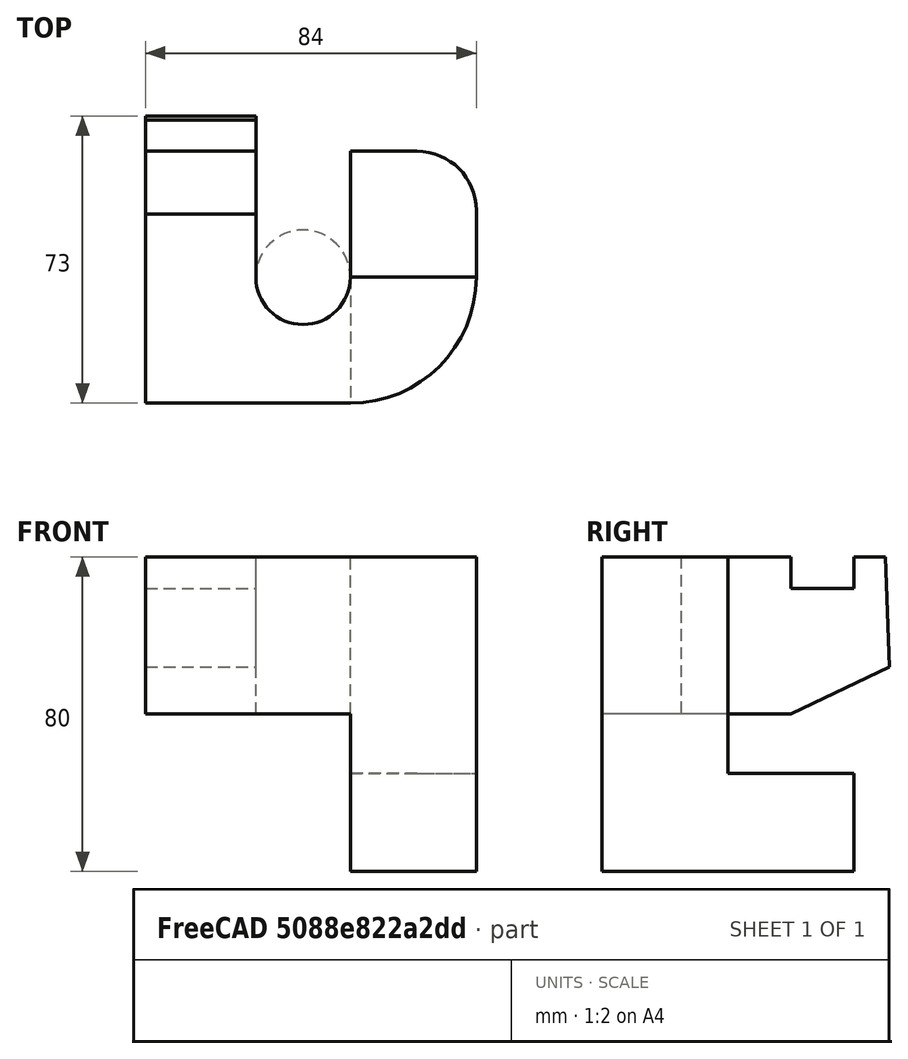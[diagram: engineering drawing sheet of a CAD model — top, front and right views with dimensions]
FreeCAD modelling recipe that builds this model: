
FCSTD DOCUMENT  (FreeCAD 0.18R4 (GitTag))
Label: Ass1 2nd sem
License: All rights reserved
LicenseURL: http://en.wikipedia.org/wiki/All_rights_reserved
objects: TechDraw::DrawViewDimension×14, Sketcher::SketchObject×4, PartDesign::Pad×4, TechDraw::DrawProjGroupItem×3, TechDraw::DrawProjGroup×3, TechDraw::DrawViewAnnotation×3, PartDesign::Pocket×1, PartDesign::Body×1, TechDraw::DrawSVGTemplate×1, TechDraw::DrawPage×1
note: 15 computed .brp shape members not serialized (recipe doc carries the construction recipe); baked Part::Feature solids carry a one-line shape summary decoded from their .brp

FEATURE [Sketcher::SketchObject] Sketch
  MapMode = 5
  Support = -> [XY_Plane]
  sketch-geometry (7):
    g0: LineSegment StartX=28 StartY=32 StartZ=0 EndX=28 EndY=48 EndZ=0
    g1: LineSegment StartX=28 StartY=48 StartZ=0 EndX=0 EndY=48 EndZ=0
    g2: LineSegment StartX=0 StartY=48 StartZ=0 EndX=0 EndY=0 EndZ=0
    g3: LineSegment StartX=0 StartY=0 StartZ=0 EndX=52 EndY=0 EndZ=0
    g4: LineSegment StartX=84 StartY=32 StartZ=0 EndX=52 EndY=32 EndZ=0
    g5: ArcOfCircle CenterX=52 CenterY=32 CenterZ=0 NormalX=0 NormalY=0 NormalZ=1 AngleXU=0 Radius=32 StartAngle=4.71239 EndAngle=6.28319
    g6: ArcOfCircle CenterX=40 CenterY=32 CenterZ=0 NormalX=0 NormalY=0 NormalZ=1 AngleXU=0 Radius=12 StartAngle=3.14159 EndAngle=6.28319
  constraints (20):
    c: Coincident(g0,g1)
    c: Coincident(g1,g2)
    c: Coincident(g2,g3)
    c: Parallel(g1,g4)
    c: Parallel(g4,g3)
    c: Parallel(g3,g-1)
    c: Parallel(g2,g0)
    c: Tangent(g3,g5) = -1.5708
    c: Coincident(g4,g5)
    c: Radius(g5) = 32
    c: Coincident(g-1,g2)
    c: PointOnObject(g1,g-2)
    c: DistanceX(g2,g4) = 84
    c: DistanceY(g2,g2) = 48
    c: DistanceX(g1,g1) = 28
    c: Coincident(g5,g4)
    c: DistanceY(g0,g0) = 16
    c: Radius(g6) = 12
    c: Coincident(g6,g4)
    c: Coincident(g6,g0)
FEATURE [PartDesign::Pad] Pad
  Length = 40
  Length2 = 100
  Profile = -> Sketch
  Type = 0
FEATURE [Sketcher::SketchObject] Sketch003
  MapMode = 5
  Placement = pos=(0,0,0) rot=(0.57735,-0.57735,-0.57735;2.0944rad)
  sketch-geometry (6):
    g0: LineSegment StartX=-48 StartY=0 StartZ=0 EndX=-73 EndY=12 EndZ=0
    g1: LineSegment StartX=-73 StartY=12 StartZ=0 EndX=-72 EndY=40 EndZ=0
    g2: LineSegment StartX=-72 StartY=40 StartZ=0 EndX=-64 EndY=40 EndZ=0
    g3: LineSegment StartX=-64 StartY=40 StartZ=0 EndX=-64 EndY=32 EndZ=0
    g4: LineSegment StartX=-64 StartY=32 StartZ=0 EndX=-48 EndY=32 EndZ=0
    g5: LineSegment StartX=-48 StartY=0 StartZ=0 EndX=-48 EndY=32 EndZ=0
  constraints (13):
    c: Coincident(g0,g1)
    c: Coincident(g1,g2)
    c: Coincident(g2,g3)
    c: Coincident(g3,g4)
    c: DistanceY(g1,g1) = 28
    c: Parallel(g2,g4)
    c: Parallel(g4,g-1)
    c: DistanceX(g2,g2) = 8
    c: DistanceY(g3,g3) = 8
    c: DistanceX(g4,g4) = 16
    c: DistanceX(g0,g0) = 25
    c: Coincident(g5,g4)
    c: Coincident(g5,g0)
FEATURE [PartDesign::Pad] Pad003
  BaseFeature = -> Pad
  Length = 28
  Length2 = 100
  Profile = -> Sketch003
  Reversed = true
  Type = 0
FEATURE [PartDesign::Pad] Pad004
  BaseFeature = -> Pad003
  Length = 40
  Length2 = 100
  Profile = -> Pad003 [Face5]
  Type = 0
FEATURE [Sketcher::SketchObject] Sketch004
  ExternalGeometry = -> [Pad004]
  MapMode = 5
  Placement = pos=(0,0,-40) rot=(1,0,0;3.14159rad)
  Support = -> [Pad004]
  sketch-geometry (6):
    g0: LineSegment StartX=52 StartY=0 StartZ=0 EndX=0 EndY=0 EndZ=0
    g1: LineSegment StartX=0 StartY=0 StartZ=0 EndX=0 EndY=-48 EndZ=0
    g2: LineSegment StartX=0 StartY=-48 StartZ=0 EndX=28 EndY=-48 EndZ=0
    g3: LineSegment StartX=28 StartY=-48 StartZ=0 EndX=28 EndY=-32 EndZ=0
    g4: LineSegment StartX=52 StartY=-32 StartZ=0 EndX=52 EndY=0 EndZ=0
    g5: ArcOfCircle CenterX=40 CenterY=-32 CenterZ=0 NormalX=0 NormalY=0 NormalZ=1 AngleXU=0 Radius=12 StartAngle=6.28318 EndAngle=9.42478
  constraints (12):
    c: Coincident(g0,g1)
    c: Coincident(g1,g2)
    c: Coincident(g2,g3)
    c: Coincident(g4,g0)
    c: Coincident(g0,g-1)
    c: Coincident(g-4,g0)
    c: Coincident(g1,g-3)
    c: Coincident(g2,g-3)
    c: Tangent(g3,g5) = 1.5708
    c: Coincident(g5,g-5)
    c: Coincident(g5,g-5)
    c: Coincident(g4,g5)
FEATURE [PartDesign::Pocket] Pocket
  BaseFeature = -> Pad004
  Length = 40
  Length2 = 100
  Profile = -> Sketch004
  Type = 0
FEATURE [Sketcher::SketchObject] Sketch005
  ExternalGeometry = -> [Pocket]
  MapMode = 5
  Placement = pos=(0,0,-40) rot=(1,0,0;3.14159rad)
  Support = -> [Pocket]
  sketch-geometry (5):
    g0: LineSegment StartX=52 StartY=-32 StartZ=0 EndX=84 EndY=-32 EndZ=0
    g1: LineSegment StartX=84 StartY=-32 StartZ=0 EndX=84 EndY=-49 EndZ=0
    g2: LineSegment StartX=69 StartY=-64 StartZ=0 EndX=52 EndY=-64 EndZ=0
    g3: LineSegment StartX=52 StartY=-64 StartZ=0 EndX=52 EndY=-32 EndZ=0
    g4: ArcOfCircle CenterX=69 CenterY=-49 CenterZ=0 NormalX=0 NormalY=0 NormalZ=1 AngleXU=0 Radius=15 StartAngle=4.71239 EndAngle=6.28319
  constraints (12):
    c: Coincident(g0,g1)
    c: Coincident(g2,g3)
    c: Coincident(g3,g0)
    c: Horizontal(g2)
    c: Vertical(g1)
    c: Vertical(g3)
    c: Tangent(g2,g4) = 1.5708
    c: Tangent(g1,g4) = 1.5708
    c: Coincident(g0,g-3)
    c: Coincident(g0,g-3)
    c: Radius(g4) = 15
    c: DistanceY(g3,g3) = 32
FEATURE [PartDesign::Pad] Pad005
  BaseFeature = -> Pocket
  Length = 25
  Length2 = 100
  Profile = -> Sketch005
  Reversed = true
  Type = 0
FEATURE [PartDesign::Body] Body
  Group = -> [Sketch,Pad,Sketch003,Pad003,Pad004,Sketch004,Pocket,Sketch005,Pad005]
  Origin = -> Origin
  Tip = -> Pad005
FEATURE [TechDraw::DrawSVGTemplate] Template
  EditableTexts = Designed_by_Name=Soumojit Shome; Drawing_number=Assignment 1; FC-Date=21/04/2023; FC-SC=1:1; FC-SH=01; FC-Title=Academy of Technology; Subtitle=ECE2 (Y) 16900322101; Weight=Weight
  Height = 210
  Orientation = 1
  Width = 297
FEATURE [TechDraw::DrawProjGroupItem] ProjItem  label="Front"
  CoarseView = false
  Direction = (0,0,1)
  Focus = 100
  HardHidden = false
  IsoCount = 0
  IsoHidden = false
  IsoVisible = false
  LockPosition = true
  Perspective = false
  Rotation = 0
  RotationVector = (1,0,0)
  ScaleType = 2
  SeamHidden = false
  SeamVisible = false
  SmoothHidden = false
  SmoothVisible = false
  Source = -> [Pad005]
  Type = 0
  X = 0
  Y = 0
FEATURE [TechDraw::DrawProjGroup] ProjGroup
  Anchor = -> ProjItem
  AutoDistribute = true
  LockPosition = false
  ProjectionType = 0
  Rotation = 0
  ScaleType = 0
  Source = -> [Pad005]
  Views = -> [ProjItem]
  X = 76.761
  Y = 159.613
  spacingX = 15
  spacingY = 15
FEATURE [TechDraw::DrawViewAnnotation] Annotation
  Font = osifont
  LineSpace = 80
  LockPosition = false
  MaxWidth = -1
  Rotation = 0
  ScaleType = 0
  Text = Front View
  TextSize = 6
  TextStyle = 0
  X = 59.4977
  Y = 110.962
FEATURE [TechDraw::DrawProjGroupItem] ProjItem001  label="Front001"
  CoarseView = false
  Direction = (0,1,0)
  Focus = 100
  HardHidden = false
  IsoCount = 0
  IsoHidden = false
  IsoVisible = false
  LockPosition = true
  Perspective = false
  Rotation = 0
  RotationVector = (1,0,0)
  ScaleType = 2
  SeamHidden = false
  SeamVisible = false
  SmoothHidden = false
  SmoothVisible = false
  Source = -> [Pad005]
  Type = 0
  X = 0
  Y = 0
FEATURE [TechDraw::DrawProjGroup] ProjGroup001
  Anchor = -> ProjItem001
  AutoDistribute = true
  LockPosition = false
  ProjectionType = 0
  Rotation = 0
  ScaleType = 0
  Source = -> [Pad005]
  Views = -> [ProjItem001]
  X = 87.969
  Y = 67.0956
  spacingX = 15
  spacingY = 15
FEATURE [TechDraw::DrawViewAnnotation] Annotation001
  Font = osifont
  LineSpace = 80
  LockPosition = false
  MaxWidth = -1
  Rotation = 0
  ScaleType = 0
  Text = Top View
  TextSize = 6
  TextStyle = 0
  X = 95.5839
  Y = 22.2392
FEATURE [TechDraw::DrawProjGroupItem] ProjItem002  label="Front002"
  CoarseView = false
  Direction = (0.489,0.5,0.715)
  Focus = 100
  HardHidden = false
  IsoCount = 0
  IsoHidden = false
  IsoVisible = false
  LockPosition = true
  Perspective = false
  Rotation = 0
  RotationVector = (0.828,-0.009,-0.56)
  ScaleType = 2
  SeamHidden = false
  SeamVisible = false
  SmoothHidden = false
  SmoothVisible = false
  Source = -> [Pad005]
  Type = 0
  X = 0
  Y = 0
FEATURE [TechDraw::DrawProjGroup] ProjGroup002
  Anchor = -> ProjItem002
  AutoDistribute = true
  LockPosition = false
  ProjectionType = 0
  Rotation = 0
  ScaleType = 0
  Source = -> [Pad005]
  Views = -> [ProjItem002]
  X = 216.563
  Y = 138.617
  spacingX = 15
  spacingY = 15
FEATURE [TechDraw::DrawViewAnnotation] Annotation002
  Font = osifont
  LineSpace = 80
  LockPosition = false
  MaxWidth = -1
  Rotation = 0
  ScaleType = 0
  Text = Isometric View
  TextSize = 6
  TextStyle = 0
  X = 217.808
  Y = 79.2688
FEATURE [TechDraw::DrawViewDimension] Dimension
  Arbitrary = false
  FormatSpec = %.2f
  LockPosition = false
  MeasureType = 1
  OverTolerance = 0
  References2D = -> [ProjItem001]
  Rotation = 0
  ScaleType = 0
  Type = 2
  UnderTolerance = 0
  X = -51.9605
  Y = -25.17
FEATURE [TechDraw::DrawViewDimension] Dimension001
  Arbitrary = false
  FormatSpec = %.2f
  LockPosition = false
  MeasureType = 1
  OverTolerance = 0
  References2D = -> [ProjItem001]
  Rotation = 0
  ScaleType = 0
  Type = 1
  UnderTolerance = 0
  X = -28
  Y = 7.47036
FEATURE [TechDraw::DrawViewDimension] Dimension002
  Arbitrary = false
  FormatSpec = %.2f
  LockPosition = false
  MeasureType = 1
  OverTolerance = 0
  References2D = -> [ProjItem]
  Rotation = 0
  ScaleType = 0
  Type = 2
  UnderTolerance = 0
  X = -61.7304
  Y = 27.6044
FEATURE [TechDraw::DrawViewDimension] Dimension003
  Arbitrary = false
  FormatSpec = %.2f
  LockPosition = false
  MeasureType = 1
  OverTolerance = 0
  References2D = -> [ProjItem]
  Rotation = 0
  ScaleType = 0
  Type = 2
  UnderTolerance = 0
  X = -8.64263
  Y = 27.9713
FEATURE [TechDraw::DrawViewDimension] Dimension004
  Arbitrary = false
  FormatSpec = %.2f
  LockPosition = false
  MeasureType = 1
  OverTolerance = 0
  References2D = -> [ProjItem]
  Rotation = 0
  ScaleType = 0
  Type = 2
  UnderTolerance = 0
  X = -48.8284
  Y = 22.1274
FEATURE [TechDraw::DrawViewDimension] Dimension005
  Arbitrary = false
  FormatSpec = %.2f
  LockPosition = false
  MeasureType = 1
  OverTolerance = 0
  References2D = -> [ProjItem]
  Rotation = 0
  ScaleType = 0
  Type = 2
  UnderTolerance = 0
  X = -57.2822
  Y = -22.067
FEATURE [TechDraw::DrawViewDimension] Dimension006
  Arbitrary = false
  FormatSpec = %.2f
  LockPosition = false
  MeasureType = 1
  OverTolerance = 0
  References2D = -> [ProjItem]
  Rotation = 0
  ScaleType = 0
  Type = 2
  UnderTolerance = 0
  X = 1.16787
  Y = 14.444
FEATURE [TechDraw::DrawViewDimension] Dimension007
  Arbitrary = false
  FormatSpec = %.2f
  LockPosition = false
  MeasureType = 1
  OverTolerance = 0
  References2D = -> [ProjItem001]
  Rotation = 0
  ScaleType = 0
  Type = 2
  UnderTolerance = 0
  X = 2.63989
  Y = 27.2547
FEATURE [TechDraw::DrawViewDimension] Dimension008
  Arbitrary = false
  FormatSpec = %.2f
  LockPosition = false
  MeasureType = 1
  OverTolerance = 0
  References2D = -> [ProjItem001]
  Rotation = 0
  ScaleType = 0
  Type = 2
  UnderTolerance = 0
  X = 44.944
  Y = -10.292
FEATURE [TechDraw::DrawViewDimension] Dimension009
  Arbitrary = false
  FormatSpec = %.2f
  LockPosition = false
  MeasureType = 1
  OverTolerance = 0
  References2D = -> [ProjItem001]
  Rotation = 0
  ScaleType = 0
  Type = 2
  UnderTolerance = 0
  X = -10.8106
  Y = -19.5093
FEATURE [TechDraw::DrawViewDimension] Dimension010
  Arbitrary = false
  FormatSpec = R%.2f
  LockPosition = false
  MeasureType = 1
  OverTolerance = 0
  References2D = -> [ProjItem]
  Rotation = 0
  ScaleType = 0
  Type = 4
  UnderTolerance = 0
  X = -23.5523
  Y = -26.7417
FEATURE [TechDraw::DrawViewDimension] Dimension011
  Arbitrary = false
  FormatSpec = R%.2f
  LockPosition = false
  MeasureType = 1
  OverTolerance = 0
  References2D = -> [ProjItem]
  Rotation = 0
  ScaleType = 0
  Type = 4
  UnderTolerance = 0
  X = 61.0889
  Y = -29.6858
FEATURE [TechDraw::DrawViewDimension] Dimension012
  Arbitrary = false
  FormatSpec = %.2f
  LockPosition = false
  MeasureType = 1
  OverTolerance = 0
  References2D = -> [ProjItem]
  Rotation = 0
  ScaleType = 0
  Type = 1
  UnderTolerance = 0
  X = -0.736011
  Y = -42.0896
FEATURE [TechDraw::DrawViewDimension] Dimension013
  Arbitrary = false
  FormatSpec = R%.2f
  LockPosition = false
  MeasureType = 1
  OverTolerance = 0
  References2D = -> [ProjItem]
  Rotation = 0
  ScaleType = 0
  Type = 4
  UnderTolerance = 0
  X = 63.456
  Y = 34.0703
FEATURE [TechDraw::DrawPage] Page
  KeepUpdated = true
  ProjectionType = 0
  Template = -> Template
  Views = -> [ProjGroup,Annotation,ProjGroup001,Annotation001,ProjGroup002,Annotation002,Dimension,Dimension001,Dimension002,Dimension003,Dimension004,Dimension005,Dimension006,Dimension007,Dimension008,Dimension009,Dimension010,Dimension011,Dimension012,Dimension013]
